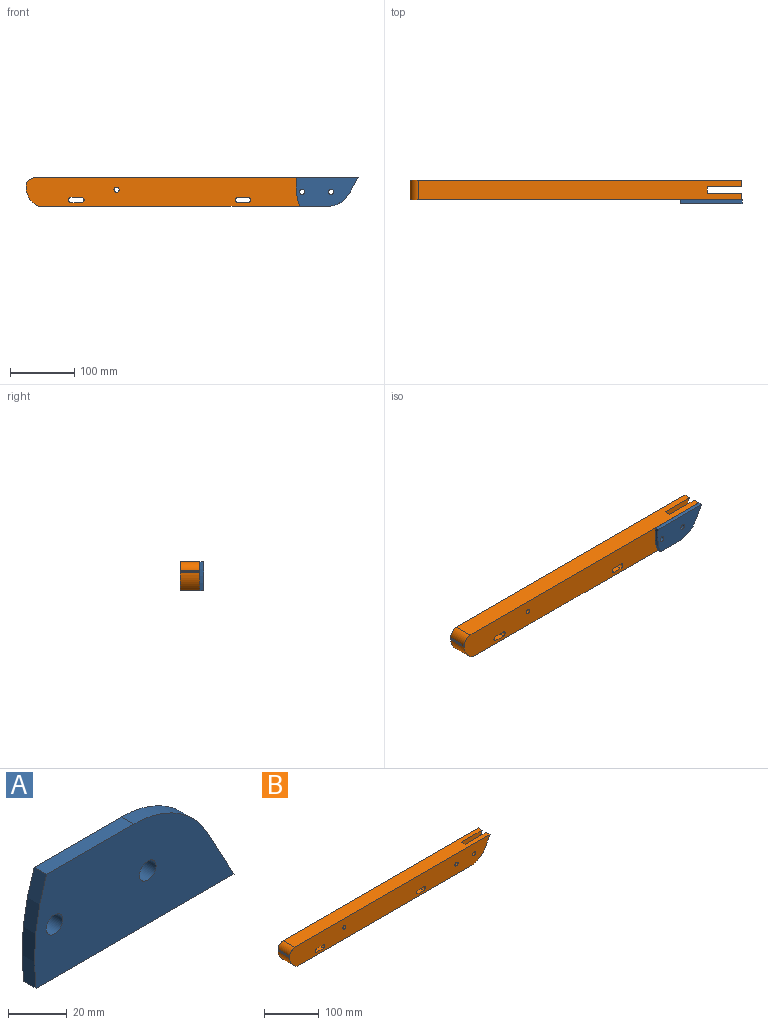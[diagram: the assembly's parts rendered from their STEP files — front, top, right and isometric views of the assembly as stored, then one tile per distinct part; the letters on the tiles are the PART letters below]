
ASSEMBLY  parts=2 mates=1
PART A: 9 faces, bbox 96.3x6x45 mm
  f0: plane 42.07x6mm, normal (0,0,1), area 252.4mm2, adj f1,f6,f7,f8
  f1: cylinder r=95mm len=45mm, axis (0,1,0), area 274.4mm2, adj f0,f2,f7,f8
  f2: plane 95.5x6mm, normal (0,0,-1), area 573mm2, adj f1,f3,f7,f8
  f3: plane 24.21x13.26mm, normal (0.88,0,0.48), area 165.6mm2, adj f2,f6,f7,f8
  f4: cylinder r=4mm len=8mm, axis (0,1,0), area 150.8mm2, adj f7,f8
  f5: cylinder r=4mm len=8mm, axis (0,1,0), area 150.8mm2, adj f7,f8
  f6: cylinder r=40mm len=35.08mm, axis (0,1,0), area 256.7mm2, adj f0,f3,f7,f8
  f7: plane 96.28x45mm, normal (0,-1,0), area 3518.7mm2, adj f0,f1,f2,f3,f4,f5,f6
  f8: plane 96.28x45mm, normal (0,1,0), area 3518.7mm2, adj f0,f1,f2,f3,f4,f5,f6
PART B: 28 faces, bbox 515.1x30x45 mm
  f0: plane 448.75x30mm, normal (0,0,-1), area 13128.5mm2, adj f1,f13,f14,f23,f24,f25,f26,f27
  f1: cylinder r=42.57mm len=35.19mm, axis (0,1,0), area 436.5mm2, adj f0,f2,f23,f26
  f2: plane 22.5x11.98mm, normal (0.88,0,-0.47), area 254.9mm2, adj f1,f3,f23,f26
  f3: plane 502.13x30mm, normal (0,0,1), area 14526.6mm2, adj f2,f15,f16,f23,f24,f25,f26,f27
  f4: cylinder r=4.31mm len=10mm, axis (0,1,0), area 270.7mm2, adj f23,f26
  f5: cylinder r=4mm len=30mm, axis (0,1,0), area 377mm2, adj f6,f22,f23,f24
  f6: plane 30x15mm, normal (0,0,-1), area 450mm2, adj f5,f7,f23,f24
  f7: cylinder r=4mm len=30mm, axis (0,1,0), area 377mm2, adj f6,f22,f23,f24
  f8: cylinder r=4mm len=30mm, axis (0,1,0), area 382.2mm2, adj f9,f17,f23,f24
  f9: plane 30x16.15mm, normal (0,0,-1), area 484.6mm2, adj f8,f10,f23,f24
  f10: cylinder r=4mm len=30mm, axis (0,1,0), area 382.2mm2, adj f9,f17,f23,f24
  f11: plane 30x1.42mm, normal (-1,0,0), area 42.6mm2, adj f12,f18,f23,f24
  f12: cylinder r=14.84mm len=30mm, axis (0,1,0), area 36.4mm2, adj f11,f13,f23,f24
  f13: cylinder r=34.88mm len=30mm, axis (0,1,0), area 1048.6mm2, adj f0,f12,f23,f24
  f14: cylinder r=42.57mm len=35.19mm, axis (0,1,0), area 436.5mm2, adj f0,f15,f24,f27
  f15: plane 22.5x11.98mm, normal (0.88,0,-0.47), area 254.9mm2, adj f3,f14,f24,f27
  f16: cylinder r=14.84mm len=30mm, axis (0,1,0), area 603.7mm2, adj f3,f18,f23,f24
  f17: plane 30x16.5mm, normal (0,0,1), area 495mm2, adj f8,f10,f23,f24
  f18: cylinder r=34.88mm len=30mm, axis (0,1,0), area 43.5mm2, adj f11,f16,f23,f24
  f19: cylinder r=4mm len=30mm, axis (0,1,0), area 754mm2, adj f23,f24
  f20: cylinder r=4mm len=30mm, axis (0,1,0), area 754mm2, adj f23,f24
  f21: cylinder r=4.31mm len=10mm, axis (0,1,0), area 270.7mm2, adj f24,f27
  f22: plane 30x15mm, normal (0,0,1), area 450mm2, adj f5,f7,f23,f24
  f23: plane 515.12x45mm, normal (0,-1,0), area 21807.9mm2, adj f0,f1,f2,f3,f4,f5,f6,f7
  f24: plane 515.12x45mm, normal (0,1,0), area 21807.9mm2, adj f0,f3,f5,f6,f7,f8,f9,f10
  f25: plane 45x26.81mm, normal (0.86,0,-0.51), area 523.8mm2, adj f0,f3,f26,f27
  f26: plane 80.55x45mm, normal (0,1,0), area 2317.9mm2, adj f0,f1,f2,f3,f4,f25
  f27: plane 80.55x45mm, normal (0,-1,0), area 2317.9mm2, adj f0,f3,f14,f15,f21,f25
PLACE A rot(axis=(-1,0,0),180deg) t=(133.28,-25.16,-103.17)mm
PLACE B t=(-169.5,10.84,-113.49)mm
MATE fastened B.f4 <-> A.f5  axis (0,-1,0) through (40.5,-19.16,-113.29)mm
